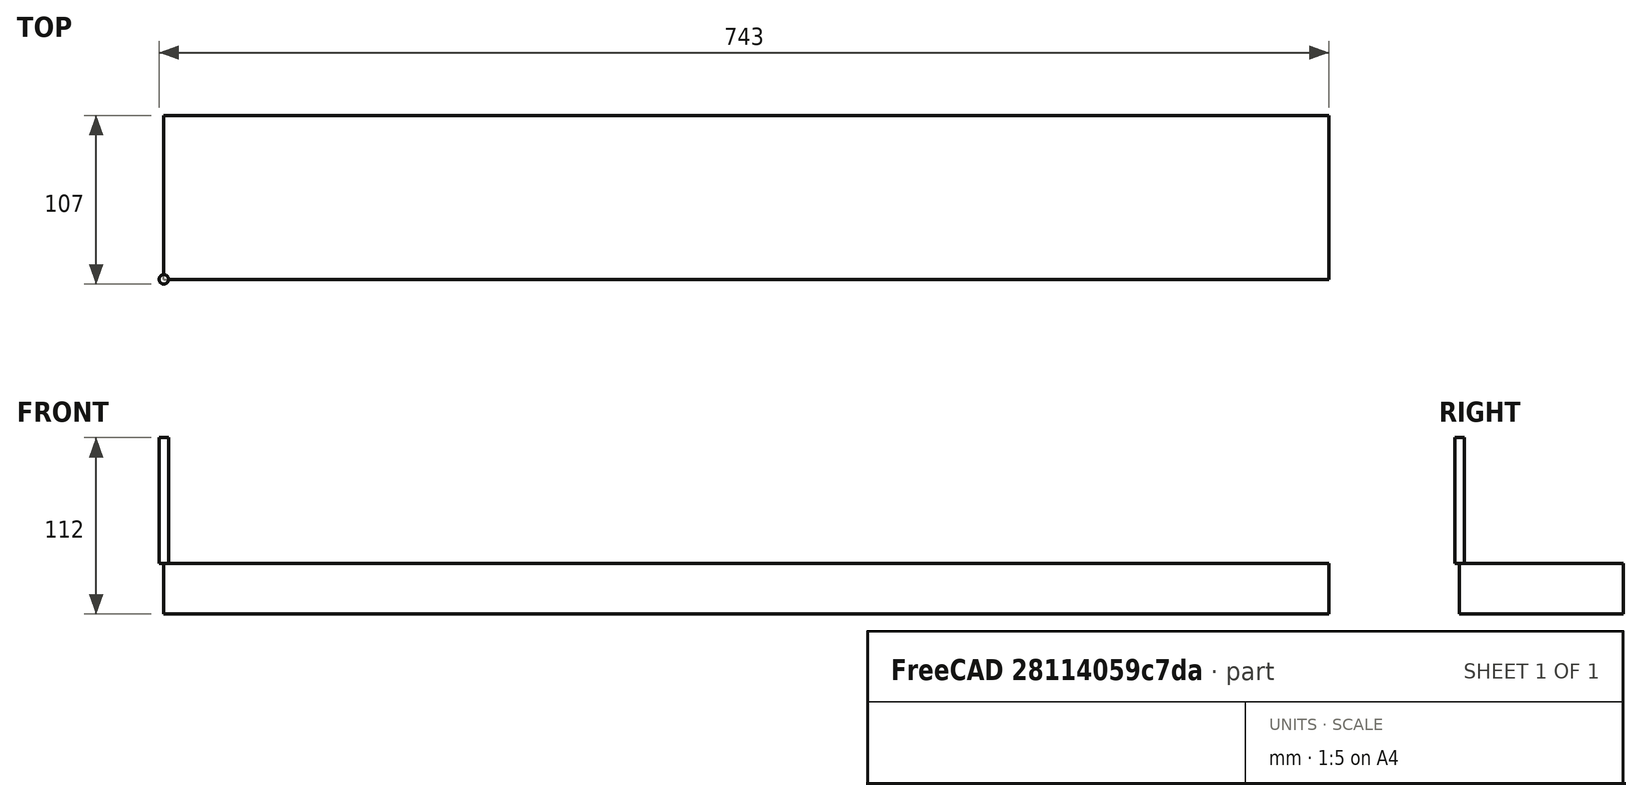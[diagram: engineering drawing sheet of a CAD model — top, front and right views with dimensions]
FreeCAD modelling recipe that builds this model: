
FCSTD DOCUMENT  (FreeCAD 0.22R34789 (Git))
Label: fence_base
License: All rights reserved
LicenseURL: http://en.wikipedia.org/wiki/All_rights_reserved
objects: Path::FeaturePython×7, Part::FeaturePython×4, App::DocumentObjectGroup×3, App::FeaturePython×1, Mesh::FeaturePython×1
note: 9 computed .brp shape members not serialized (recipe doc carries the construction recipe); baked Part::Feature solids carry a one-line shape summary decoded from their .brp

FEATURE [Part::FeaturePython] b_drill_press_table_001_  label="drill_press_table_fence_base_001"  # a2plus imported part (geometry in sourceFile) (typed FeaturePython)
  Placement = pos=(0,0,0) rot=(1,0,0;3.14159rad)
  a2p_Version = 0.4.61
  fixedPosition = true
  objectType = a2pPart
  sourceFile = ./../drill_press_table.FCStd
  sourcePart = fence_base
  subassemblyImport = false
  timeLastImport = 1.69948e+09
  updateColors = true
FEATURE [App::FeaturePython] SetupSheet  # Path/CAM operation (typed FeaturePython)
  ClearanceHeightExpression = OpStockZMax+SetupSheet.ClearanceHeightOffset
  ClearanceHeightOffset = 5
  CoolantMode = 0
  CoolantModes = None | Flood | Mist
  FinalDepthExpression = OpFinalDepth
  HorizRapid = 0
  SafeHeightExpression = OpStockZMax+SetupSheet.SafeHeightOffset
  SafeHeightOffset = 3
  StartDepthExpression = OpStartDepth
  StepDownExpression = OpToolDiameter
  VertRapid = 0
FEATURE [Part::FeaturePython] Clone  label="Model-drill_press_table_fence_base_001"  # Draft clone (typed FeaturePython)
  AttacherType = Attacher::AttachEngine3D
  Fuse = false
  Objects = -> [b_drill_press_table_001_]
  PathResource = Model
  Placement = pos=(370,394,36) rot=(1,0,0;3.14159rad)
  Scale = (1,1,1)
FEATURE [App::DocumentObjectGroup] Model
  Group = -> [Clone]
FEATURE [Part::FeaturePython] Stock  # WARN: FeaturePython — macro-defined, semantics opaque (R4)
  Base = -> Model
  ExtXneg = 10
  ExtXpos = 10
  ExtYneg = 10
  ExtYpos = 10
  ExtZneg = 0
  ExtZpos = 0
  Placement = pos=(10,10,-32) rot=(0,0,1;0rad)
  StockType = FromBase
FEATURE [Part::FeaturePython] ToolBit001  label="6 mm endmill, D=6, H=45, L=80, S=6"  # Path/CAM toolbit (typed FeaturePython)
  BitPropertyNames = Chipload | CuttingEdgeHeight | Diameter | Flutes | Length | Material | ShankDiameter | SpindleDirection
  BitShape = <userpath>/.local/share/FreeCAD/Macro/Tools/Shape/endmill.fcstd
  Chipload = 0
  CuttingEdgeHeight = 45
  Diameter = 6
  File = <userpath>/.local/share/FreeCAD/Macro/Tools/Bit/03c10998-7ce6-11ee-8713-1065300da2fe.fctb
  Flutes = 2
  Length = 80
  Material = 1
  ShankDiameter = 6
  ShapeName = endmill
  SpindleDirection = 0
FEATURE [Path::FeaturePython] TC__6_mm_endmill__D_6__H_45__L_80__S_6  label="TC: 6 mm endmill, D=6, H=45, L=80, S=6"  # Path/CAM operation (typed FeaturePython)
  HorizFeed = 10
  HorizRapid = 0
  SpindleDir = 0
  SpindleSpeed = 0
  Tool = -> ToolBit001
  ToolNumber = 17
  VertFeed = 1
  VertRapid = 0
  expr: HorizRapid = SetupSheet.HorizRapid
  expr: VertRapid = SetupSheet.VertRapid
FEATURE [App::DocumentObjectGroup] Tools
  Group = -> [TC__6_mm_endmill__D_6__H_45__L_80__S_6]
FEATURE [Path::FeaturePython] Pocket_Shape  # Path/CAM operation (typed FeaturePython)
  Active = true
  AreaParams:
    Tolerance = 1e-07
    FitArcs = True
    Simplify = False
    CleanDistance = 0.0
    Accuracy = 0.01
    Unit = 1.0
    MinArcPoints = 4
    MaxArcPoints = 100
    ClipperScale = 10000000.0
    Fill = 0
    Coplanar = 0
    Reorient = True
    Outline = False
    Explode = False
    OpenMode = 0
    Deflection = 0.01
    SubjectFill = 0
    ClipFill = 0
    Offset = 0.0
    ExtraPass = 0
    Stepover = 0.0
    LastStepover = 0.0
    JoinType = 0
    EndType = 0
    MiterLimit = 2.0
    RoundPrecision = 0.0
    PocketMode = 2
    ToolRadius = 3.0
    PocketExtraOffset = 0.0
    PocketStepover = 4.800000000000001
    PocketLastStepover = 0.0
    FromCenter = True
    Angle = 45.0
    AngleShift = 0.0
    Shift = 0.0
    Thicken = False
    SectionCount = -1
    Stepdown = 1.0
    SectionOffset = 0.0
    SectionTolerance = 1e-07
    SectionMode = 2
    Project = False
  Base = -> [Clone]
  ClearanceHeight = 5
  CoolantMode = 0
  CutMode = 0
  CycleTime = 00:24:39
  ExtensionCorners = true
  ExtensionFeature = -> [Clone]
  ExtensionLengthDefault = 3
  ExtraOffset = 0
  FinalDepth = -16
  FinishDepth = 0
  KeepToolDown = false
  MinTravel = false
  OffsetPattern = 1
  OpFinalDepth = -16
  OpStartDepth = 3.2e-15
  OpStockZMax = -7.1e-15
  OpStockZMin = -32
  OpToolDiameter = 6
  PathParams = {'orientation': 1, 'feedrate': 10.0, 'feedrate_v': 1.0, 'verbose': True, 'resume_height': 2.999999999999993, 'retraction': 4.999999999999993, 'return_end': True, 'preamble': False}
  PocketLastStepOver = 0
  SafeHeight = 3
  SplitArcs = false
  StartAt = 0
  StartDepth = 3.2e-15
  StartPoint = (0,0,0)
  StepDown = 2
  StepOver = 80
  ToolController = -> TC__6_mm_endmill__D_6__H_45__L_80__S_6
  UseOutline = false
  UseRestMachining = false
  UseStartPoint = false
  ZigZagAngle = 45
  expr: ClearanceHeight = OpStockZMax + SetupSheet.ClearanceHeightOffset
  expr: ExtensionLengthDefault = OpToolDiameter / 2
  expr: FinalDepth = OpFinalDepth
  expr: SafeHeight = OpStockZMax + SetupSheet.SafeHeightOffset
  expr: StartDepth = OpStartDepth
  expr: StepDown = OpToolDiameter / 3
FEATURE [Path::FeaturePython] Profile  # Path/CAM operation (typed FeaturePython)
  Active = true
  AreaParams:
    Tolerance = 1e-07
    FitArcs = True
    Simplify = False
    CleanDistance = 0.0
    Accuracy = 0.01
    Unit = 1.0
    MinArcPoints = 4
    MaxArcPoints = 100
    ClipperScale = 10000000.0
    Fill = 0
    Coplanar = 0
    Reorient = True
    Outline = False
    Explode = False
    OpenMode = 0
    Deflection = 0.01
    SubjectFill = 0
    ClipFill = 0
    Offset = -2.4
    ExtraPass = 0
    Stepover = 0.0
    LastStepover = 0.0
    JoinType = 0
    EndType = 0
    MiterLimit = 2.0
    RoundPrecision = 0.0
    PocketMode = 0
    ToolRadius = 1.0
    PocketExtraOffset = 0.0
    PocketStepover = 0.0
    PocketLastStepover = 0.0
    FromCenter = False
    Angle = 45.0
    AngleShift = 0.0
    Shift = 0.0
    Thicken = False
    SectionCount = -1
    Stepdown = 1.0
    SectionOffset = 0.0
    SectionTolerance = 1e-07
    SectionMode = 2
    Project = False
  Base = -> [Clone]
  ClearanceHeight = 5
  CoolantMode = 0
  CycleTime = 00:02:18
  Direction = 0
  FinalDepth = -33.5
  HandleMultipleFeatures = 0
  JoinType = 0
  MiterLimit = 0.1
  OffsetExtra = -0.6
  OpFinalDepth = -32
  OpStartDepth = -7.1e-15
  OpStockZMax = -7.1e-15
  OpStockZMin = -32
  OpToolDiameter = 6
  PathParams = {'orientation': 1, 'feedrate': 10.0, 'feedrate_v': 1.0, 'verbose': True, 'resume_height': 2.999999999999993, 'retraction': 4.999999999999993, 'return_end': True, 'preamble': False}
  SafeHeight = 3
  Side = 1
  SplitArcs = false
  StartDepth = -7.1e-15
  StartPoint = (0,0,0)
  StepDown = 3
  ToolController = -> TC__6_mm_endmill__D_6__H_45__L_80__S_6
  UseComp = true
  UseStartPoint = false
  processCircles = false
  processHoles = false
  processPerimeter = true
  expr: ClearanceHeight = OpStockZMax + SetupSheet.ClearanceHeightOffset
  expr: FinalDepth = OpFinalDepth - 1.5 mm
  expr: SafeHeight = OpStockZMax + SetupSheet.SafeHeightOffset
  expr: StartDepth = OpStartDepth
  expr: StepDown = OpToolDiameter / 2
FEATURE [Path::FeaturePython] Profile002  # Path/CAM operation (typed FeaturePython)
  Active = true
  AreaParams:
    Tolerance = 1e-07
    FitArcs = True
    Simplify = False
    CleanDistance = 0.0
    Accuracy = 0.01
    Unit = 1.0
    MinArcPoints = 4
    MaxArcPoints = 100
    ClipperScale = 10000000.0
    Fill = 0
    Coplanar = 0
    Reorient = True
    Outline = False
    Explode = False
    OpenMode = 0
    Deflection = 0.01
    SubjectFill = 0
    ClipFill = 0
    Offset = 3.0
    ExtraPass = 0
    Stepover = 0.0
    LastStepover = 0.0
    JoinType = 0
    EndType = 0
    MiterLimit = 2.0
    RoundPrecision = 0.0
    PocketMode = 0
    ToolRadius = 1.0
    PocketExtraOffset = 0.0
    PocketStepover = 0.0
    PocketLastStepover = 0.0
    FromCenter = False
    Angle = 45.0
    AngleShift = 0.0
    Shift = 0.0
    Thicken = False
    SectionCount = -1
    Stepdown = 1.0
    SectionOffset = 0.0
    SectionTolerance = 1e-07
    SectionMode = 2
    Project = False
  ClearanceHeight = 5
  CoolantMode = 0
  CycleTime = 00:47:22
  Direction = 0
  FinalDepth = -33.5
  HandleMultipleFeatures = 0
  JoinType = 0
  MiterLimit = 0.1
  OffsetExtra = 0
  OpFinalDepth = -32
  OpStartDepth = -7.1e-15
  OpStockZMax = -7.1e-15
  OpStockZMin = -32
  OpToolDiameter = 6
  PathParams = {'orientation': 1, 'feedrate': 10.0, 'feedrate_v': 1.0, 'verbose': True, 'resume_height': 2.999999999999993, 'retraction': 4.999999999999993, 'return_end': True, 'preamble': False}
  SafeHeight = 3
  Side = 0
  SplitArcs = false
  StartDepth = -7.1e-15
  StartPoint = (0,0,0)
  StepDown = 2
  ToolController = -> TC__6_mm_endmill__D_6__H_45__L_80__S_6
  UseComp = true
  UseStartPoint = false
  processCircles = false
  processHoles = false
  processPerimeter = true
  expr: ClearanceHeight = OpStockZMax + SetupSheet.ClearanceHeightOffset
  expr: FinalDepth = OpFinalDepth - 1.5 mm
  expr: SafeHeight = OpStockZMax + SetupSheet.SafeHeightOffset
  expr: StartDepth = OpStartDepth
  expr: StepDown = OpToolDiameter / 3
FEATURE [Path::FeaturePython] DressupTag  # Path/CAM operation (typed FeaturePython)
  Angle = 45
  Base = -> Profile002
  Height = 10
  Positions = (6) [(130,97,-33.5),(370,97,-33.5),(610,97,-33.5),(586.058,7.00067,-33.5),(370.035,7.0004,-33.5),(154.012,7.00013,-33.5)]
  Radius = 0
  SegmentationFactor = 50
  Width = 16
FEATURE [Path::FeaturePython] Profile003  # Path/CAM operation (typed FeaturePython)
  Active = true
  AreaParams:
    Tolerance = 1e-07
    FitArcs = True
    Simplify = False
    CleanDistance = 0.0
    Accuracy = 0.01
    Unit = 1.0
    MinArcPoints = 4
    MaxArcPoints = 100
    ClipperScale = 10000000.0
    Fill = 0
    Coplanar = 0
    Reorient = True
    Outline = False
    Explode = False
    OpenMode = 0
    Deflection = 0.01
    SubjectFill = 0
    ClipFill = 0
    Offset = -2.4
    ExtraPass = 0
    Stepover = 0.0
    LastStepover = 0.0
    JoinType = 0
    EndType = 0
    MiterLimit = 2.0
    RoundPrecision = 0.0
    PocketMode = 0
    ToolRadius = 1.0
    PocketExtraOffset = 0.0
    PocketStepover = 0.0
    PocketLastStepover = 0.0
    FromCenter = False
    Angle = 45.0
    AngleShift = 0.0
    Shift = 0.0
    Thicken = False
    SectionCount = -1
    Stepdown = 1.0
    SectionOffset = 0.0
    SectionTolerance = 1e-07
    SectionMode = 2
    Project = False
  Base = -> [Clone]
  ClearanceHeight = 5
  CoolantMode = 0
  CycleTime = 00:02:38
  Direction = 0
  FinalDepth = -33.5
  HandleMultipleFeatures = 0
  JoinType = 0
  MiterLimit = 0.1
  OffsetExtra = -0.6
  OpFinalDepth = -32
  OpStartDepth = -7.1e-15
  OpStockZMax = -7.1e-15
  OpStockZMin = -32
  OpToolDiameter = 6
  PathParams = {'orientation': 1, 'feedrate': 10.0, 'feedrate_v': 1.0, 'verbose': True, 'resume_height': 2.999999999999993, 'retraction': 4.999999999999993, 'return_end': True, 'preamble': False}
  SafeHeight = 3
  Side = 1
  SplitArcs = false
  StartDepth = -7.1e-15
  StartPoint = (0,0,0)
  StepDown = 3
  ToolController = -> TC__6_mm_endmill__D_6__H_45__L_80__S_6
  UseComp = true
  UseStartPoint = false
  processCircles = false
  processHoles = false
  processPerimeter = true
  expr: ClearanceHeight = OpStockZMax + SetupSheet.ClearanceHeightOffset
  expr: FinalDepth = OpFinalDepth - 1.5 mm
  expr: SafeHeight = OpStockZMax + SetupSheet.SafeHeightOffset
  expr: StartDepth = OpStartDepth
  expr: StepDown = OpToolDiameter / 2
FEATURE [App::DocumentObjectGroup] Operations
  Group = -> [Profile,Profile003,Pocket_Shape,DressupTag]
FEATURE [Path::FeaturePython] Job  # Path/CAM operation (typed FeaturePython)
  CycleTime = 01:16:57
  Fixtures = G54
  GeometryTolerance = 0.01
  JobType = 0
  Model = -> Model
  Operations = -> Operations
  OrderOutputBy = 0
  PostProcessor = 3
  PostProcessorOutputFile = %D/%d
  SetupSheet = -> SetupSheet
  SplitOutput = false
  Stock = -> Stock
  Tools = -> Tools
FEATURE [Mesh::FeaturePython] CutMaterial  # WARN: FeaturePython — macro-defined, semantics opaque (R4)
